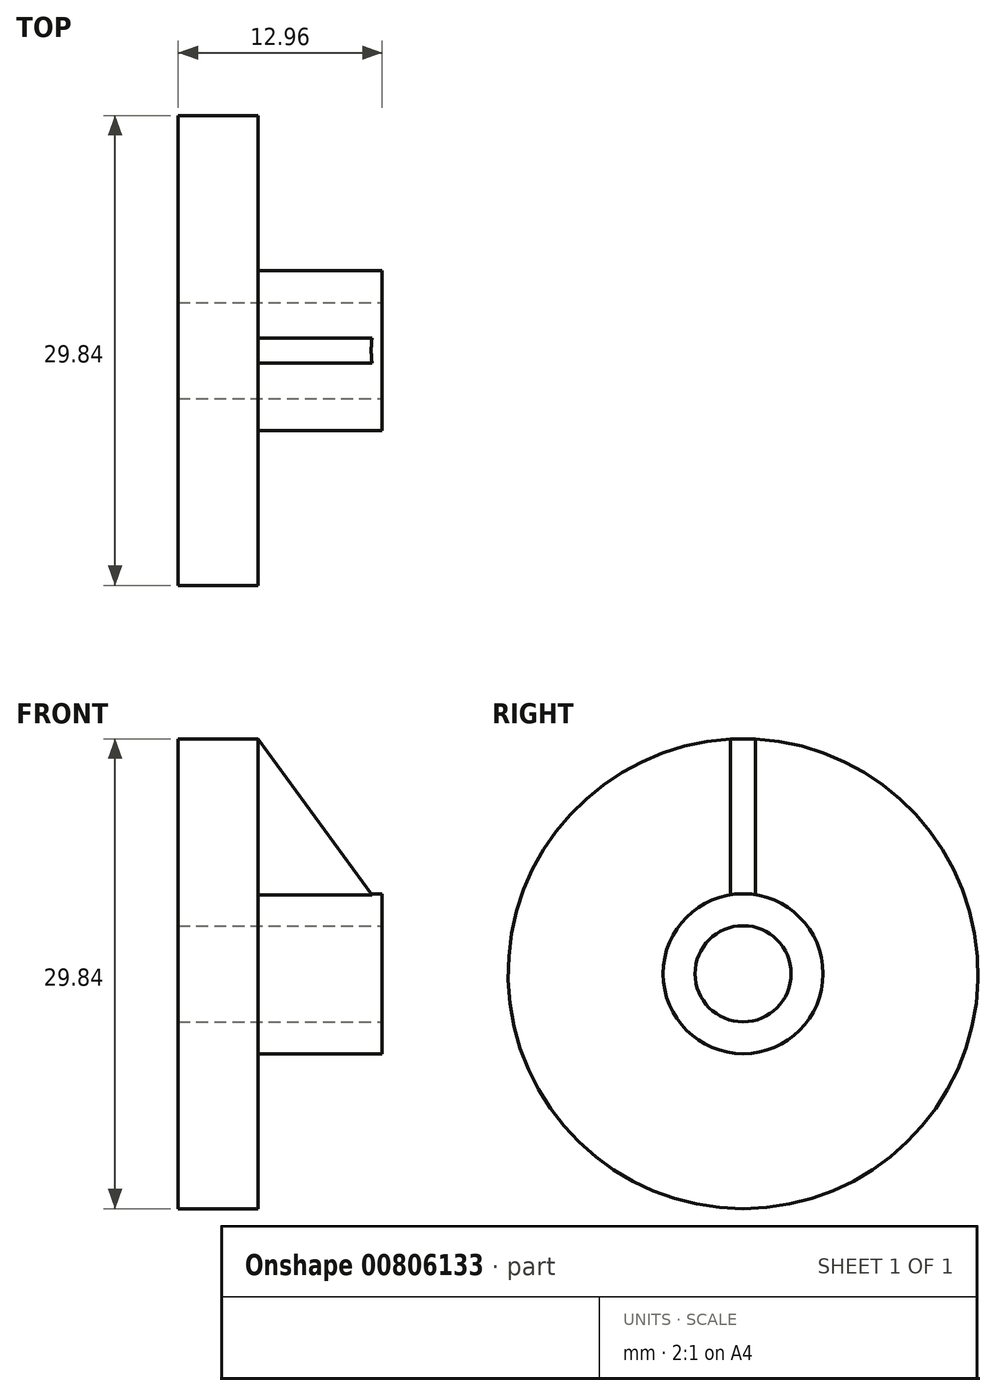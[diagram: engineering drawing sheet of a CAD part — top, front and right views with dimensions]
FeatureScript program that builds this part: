
annotation { "Feature Type Name" : "Feature", "Feature Type Description" : "" }
export const myFeature = defineFeature(function(context is Context, id is Id, definition is map)
    precondition{}
    {
        {
            var Q0;
            Q0=qCreatedBy(makeId("Top.planeOp"),FACE);
            var sketch = newSketch(context, id + "F0", { "sketchPlane" : qUnion([Q0])});
            skLineSegment(sketch, "E0", {"start": v(0, 0) * mm, "end": v(0, 3.18) * mm});
            skLineSegment(sketch, "E1", {"start": v(0, 3.18) * mm, "end": v(2.92, 3.18) * mm});
            skLineSegment(sketch, "E2", {"start": v(2.92, 3.18) * mm, "end": v(2.92, 14.92) * mm});
            skLineSegment(sketch, "E3", {"start": v(2.92, 14.92) * mm, "end": v(8, 14.92) * mm});
            skLineSegment(sketch, "E4", {"start": v(8, 14.92) * mm, "end": v(8, 5.08) * mm});
            skLineSegment(sketch, "E5", {"start": v(8, 5.08) * mm, "end": v(15.88, 5.08) * mm});
            skLineSegment(sketch, "E6", {"start": v(15.88, 5.08) * mm, "end": v(15.88, 0) * mm});
            skLineSegment(sketch, "E7", {"start": v(15.88, 0) * mm, "end": v(0, 0) * mm});
            skSolve(sketch);
        }
        {
            var Q0;
            Q0 = qSketchRegion(id + "F0", true);
            var Q1;
            Q1=sQuery(id+"F0.wireOp",EDGE,"E7");
            revolve(context, id + "F1", {"surfaceOperationType" : NewSurfaceOperationType.NEW, "entities" : qUnion([Q0]), "axis" : qUnion([Q1]), "revolveType" : RevolveType.FULL});
        }
        {
            var Q0;
            Q0=makeQuery(id+"F1.opRevolve","SWEPT_FACE",FACE,{"disambiguationData":[OSD([sQuery(id+"F0.wireOp",EDGE,"E6")])]});
            var sketch = newSketch(context, id + "F2", { "sketchPlane" : qUnion([Q0])});
            skCircle(sketch, "E8", {"center": v(0, 0) * mm, "radius": 3.05 * mm});
            skSolve(sketch);
        }
        {
            var Q0;
            Q0 = qSketchRegion(id + "F2", true);
            extrude(context, id + "F3", {"entities" : qUnion([Q0]), "operationType" : NewBodyOperationType.REMOVE, "endBound" : BoundingType.UP_TO_NEXT, "oppositeDirection" : true, "depth" : 19.05 * mm, "offsetDistance" : 25.4 * mm});
        }
        {
            var Q0;
            Q0=qCreatedBy(makeId("Front.planeOp"),FACE);
            var sketch = newSketch(context, id + "F4", { "sketchPlane" : qUnion([Q0])});
            skLineSegment(sketch, "E9.0", {"start": v(8, 14.92) * mm, "end": v(8, -14.92) * mm});
            skLineSegment(sketch, "E10", {"start": v(8, 4.13) * mm, "end": v(15.88, 4.13) * mm});
            skLineSegment(sketch, "E11", {"start": v(8, 14.92) * mm, "end": v(15.88, 4.13) * mm});
            skSolve(sketch);
        }
        {
            var Q0;
            Q0 = qSketchRegion(id + "F4", true);
            extrude(context, id + "F5", {"entities" : qUnion([Q0]), "operationType" : NewBodyOperationType.ADD, "depth" : 0.8 * mm, "offsetDistance" : 25.4 * mm, "hasSecondDirection" : true, "secondDirectionOppositeDirection" : true, "secondDirectionDepth" : 0.8 * mm});
        }
        {
            var Q0;
            Q0=makeQuery(id+"F1.opRevolve","SWEPT_FACE",FACE,{"disambiguationData":[OSD([sQuery(id+"F0.wireOp",EDGE,"E0")])]});
            var sketch = newSketch(context, id + "F6", { "sketchPlane" : qUnion([Q0])});
            skCircle(sketch, "E12.0", {"center": v(0, 0) * mm, "radius": 3.18 * mm});
            skSolve(sketch);
        }
        {
            var Q0;
            Q0 = qSketchRegion(id + "F6", true);
            var Q1;
            Q1=makeQuery(id+"F1.opRevolve","SWEPT_FACE",FACE,{"disambiguationData":[OSD([sQuery(id+"F0.wireOp",EDGE,"E2")])]});
            extrude(context, id + "F7", {"entities" : qUnion([Q0]), "operationType" : NewBodyOperationType.REMOVE, "endBound" : BoundingType.UP_TO_SURFACE, "oppositeDirection" : true, "depth" : 25.4 * mm, "endBoundEntityFace" : qUnion([Q1]), "offsetDistance" : 25.4 * mm});
        }
    });
